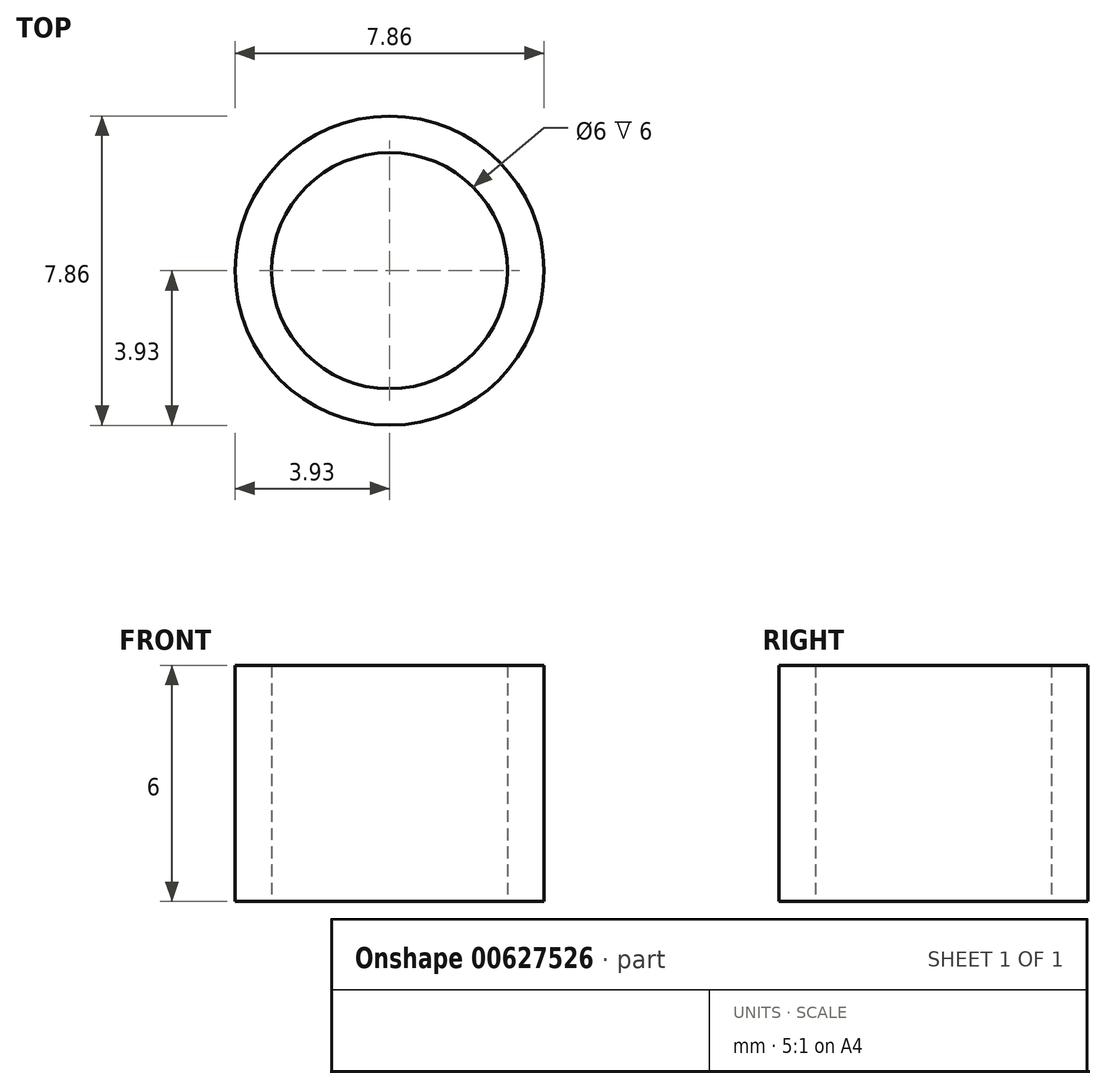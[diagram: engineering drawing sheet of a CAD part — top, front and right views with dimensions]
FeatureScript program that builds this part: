
annotation { "Feature Type Name" : "Feature", "Feature Type Description" : "" }
export const myFeature = defineFeature(function(context is Context, id is Id, definition is map)
    precondition{}
    {
        {
            var Q0;
            Q0=qCreatedBy(makeId("Top.planeOp"),FACE);
            var sketch = newSketch(context, id + "F0", { "sketchPlane" : qUnion([Q0])});
            skCircle(sketch, "E0", {"center": v(0, 0) * mm, "radius": 3 * mm});
            skCircle(sketch, "E1", {"center": v(0, 0) * mm, "radius": 3.92 * mm});
            skSolve(sketch);
        }
        {
            var Q0;
            Q0=makeQuery(id+"F0.imprint","IMPRINT",FACE,{"disambiguationData":[TD([[makeQuery(id+"F0.imprint","IMPRINT",EDGE,{"derivedFrom":sQuery(id+"F0.wireOp",EDGE,"E0")}),-1.0]])]});
            extrude(context, id + "F1", {"entities" : qUnion([Q0]), "depth" : 6 * mm, "offsetDistance" : 25 * mm});
        }
    });
